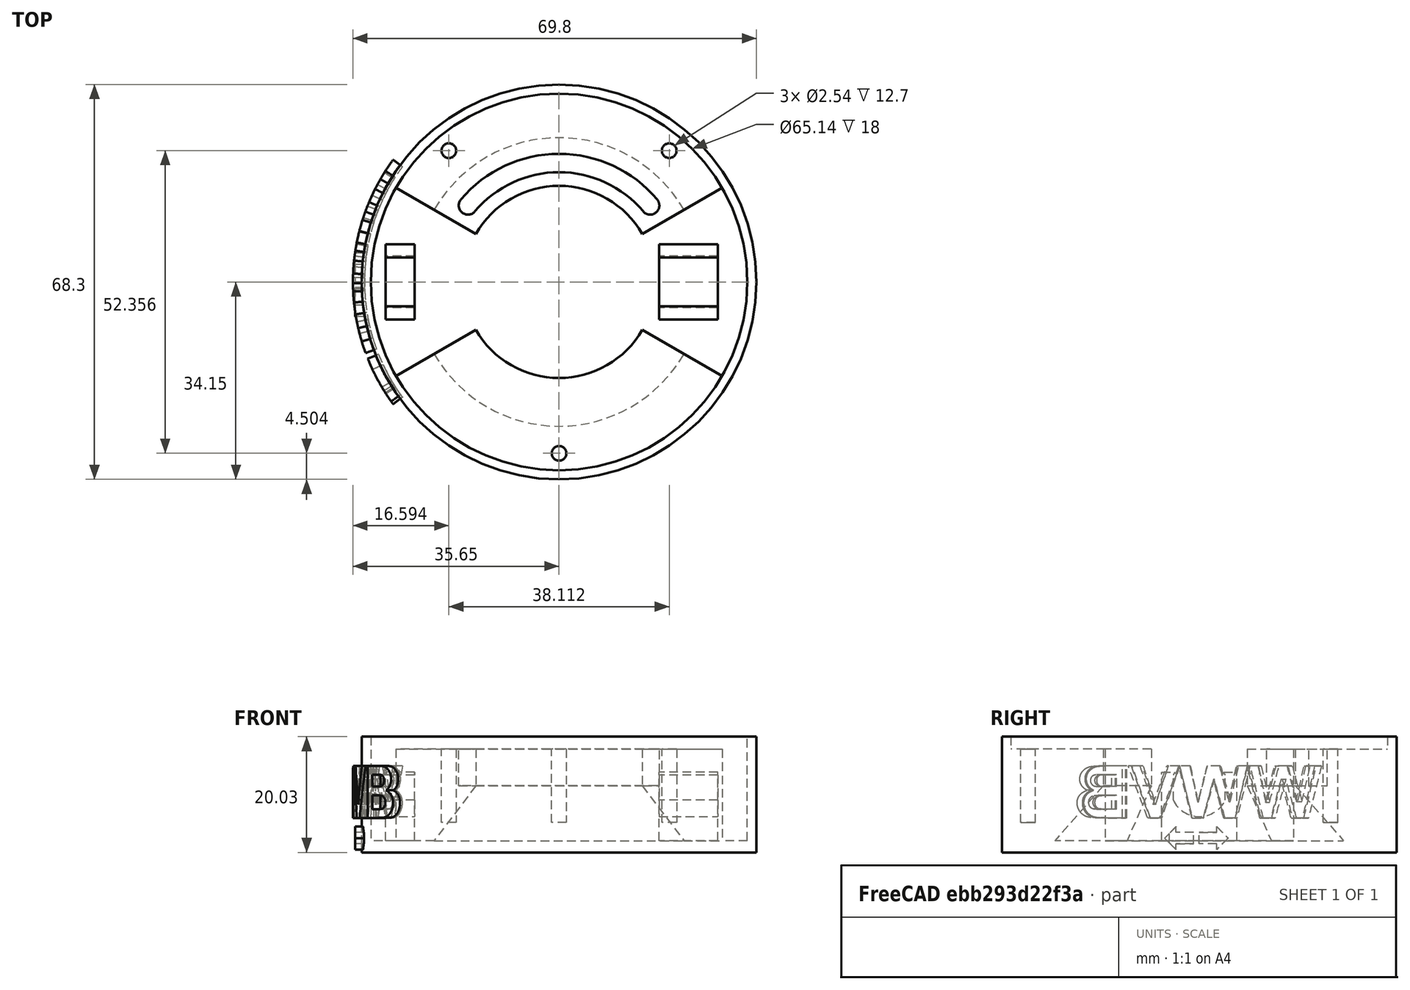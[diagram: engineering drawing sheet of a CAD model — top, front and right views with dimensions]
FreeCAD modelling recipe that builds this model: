
FCSTD DOCUMENT  (FreeCAD 1.0R39109 (Git))
Label: LetteredBase
License: All rights reserved
LicenseURL: https://en.wikipedia.org/wiki/All_rights_reserved
objects: Part::Part2DObjectPython×3, Part::Extrusion×2, PartDesign::SubShapeBinder×1, App::DocumentObjectGroup×1, Part::ProjectOnSurface×1, Part::FeaturePython×1, Part::Feature×1, Part::MultiFuse×1
note: 10 computed .brp shape members not serialized (recipe doc carries the construction recipe); baked Part::Feature solids carry a one-line shape summary decoded from their .brp
EXTERNAL_REF file=WWVBclockEnclosure.FCStd obj=Body

FEATURE [PartDesign::SubShapeBinder] Binder
  BindCopyOnChange = 0
  BindMode = 0
  ClaimChildren = false
  Fuse = false
  MakeFace = true
  OffsetFill = false
  OffsetIntersection = false
  OffsetJoinType = 0
  OffsetOpenResult = false
  PartialLoad = false
  Refine = true
  Relative = true
  Support = -> [<external WWVBclockEnclosure.FCStd>#Body]
  _Version = 2
FEATURE [Part::Part2DObjectPython] ShapeString001  # Draft 2D object (typed FeaturePython)
  FontFile = <path>
  Fuse = false
  Justification = 4
  JustificationReference = 0
  KeepLeftMargin = false
  MakeFace = true
  ObliqueAngle = 0
  Placement = pos=(-40,0,-49) rot=(0.57735,-0.57735,-0.57735;2.0944rad)
  ScaleToSize = true
  Size = 9
  String = WWVB
  Tracking = 0
FEATURE [Part::Part2DObjectPython] Wire  # Draft 2D object (typed FeaturePython)
  Area = 10
  AttachmentOffset = pos=(21,1,0) rot=(0,0,1;0rad)
  ChamferSize = 0
  Closed = true
  End = (-35.5,-1,-58)
  FilletRadius = 0
  Length = 15.6569
  MakeFace = true
  MapMode = 2
  Placement = pos=(-35.5,-1,-56) rot=(0.57735,-0.57735,-0.57735;2.0944rad)
  Points = (7) [(0,0,0),(3,0,0),(3,1,0),(5,-1,0),(3,-3,0),(3,-2,0),(0,-2,0)]
  Start = (-35.5,-1,-56)
  Subdivisions = 0
FEATURE [Part::Part2DObjectPython] Wire001  # Draft 2D object (typed FeaturePython)
  Area = 10
  AttachmentOffset = pos=(-1,0,0) rot=(0,0,1;0rad)
  AttachmentSupport = -> [Wire]
  ChamferSize = 0
  Closed = true
  End = (-35.5,0,-58)
  FilletRadius = 0
  Length = 15.6569
  MakeFace = true
  MapMode = 2
  Placement = pos=(-35.5,0,-56) rot=(0.57735,-0.57735,-0.57735;2.0944rad)
  Points = (7) [(0,0,0),(-3,0,0),(-3,1,0),(-5,-1,0),(-3,-3,0),(-3,-2,0),(0,-2,0)]
  Start = (-35.5,0,-56)
  Subdivisions = 0
FEATURE [App::DocumentObjectGroup] Draft_Construction  label="Construction"
  Group = -> [ShapeString001,Wire,Wire001]
FEATURE [Part::ProjectOnSurface] Projection
  Direction = (1,0,0)
  Height = 0
  Mode = 0
  Projection = -> [Wire001,ShapeString001,Wire]
  SupportFace = -> Binder [Face30]
FEATURE [Part::FeaturePython] Facebinder  # WARN: FeaturePython — macro-defined, semantics opaque (R4)
  Area = 201.071
  Extrusion = 2
  Faces = -> [Projection]
  Offset = -0.5
  RemoveSplitter = false
  Sew = false
FEATURE [Part::Extrusion] Extrude
  Base = -> Wire
  Dir = (-1,0,0)
  DirMode = 2
  FaceMakerClass = Part::FaceMakerBullseye
  FaceMakerMode = 3
  LengthFwd = 1.5
  LengthRev = 0
  Solid = false
  Symmetric = false
FEATURE [Part::Extrusion] Extrude001
  Base = -> Wire001
  Dir = (-1,0,0)
  DirMode = 2
  FaceMakerClass = Part::FaceMakerBullseye
  FaceMakerMode = 3
  LengthFwd = 1.5
  LengthRev = 0
  Solid = false
  Symmetric = false
FEATURE [Part::Feature] Facebinder_solid  label="Facebinder (Solid)"
  shape: bbox 8.553 x 42.26 x 9 mm, 74 faces (baked)
FEATURE [Part::MultiFuse] Fusion  label="LetteredBase"
  Refine = true
  Shapes = -> [Facebinder_solid,Extrude001,Extrude,Binder]
note: 1 file-system path scrubbed to <path> (originals preserved in the JSON sidecar)
